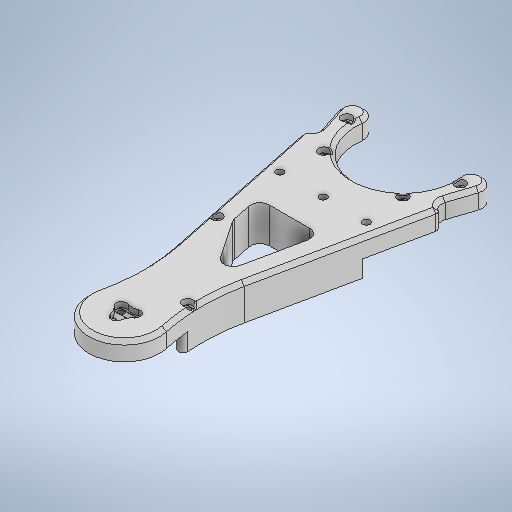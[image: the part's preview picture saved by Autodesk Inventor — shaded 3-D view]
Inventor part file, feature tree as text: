
AUTODESK INVENTOR PART (.ipt)
format: ipt  version: 2025.2 (Build 292293000, 293)  size: 1,431,040 bytes
history: native  units: mm
features: sketch x17, extrude x15, projected_geometry x11, other x8, reference x6, chamfer x2, fillet x2
ambient origin geometry x8: Origin, YZ Plane, XZ Plane, XY Plane, X Axis, Y Axis, Z Axis, Center Point
bodies: Solid1 (feature_tree)
feature tree (61):
  other  "motion_thigh_top"
  extrude  "Extrusion1"  Depth=52.1mm
  sketch  "Sketch2"  dims[d2=4.0mm d3=6.34888mm]
  extrude  "Extrusion4"  Depth=6.34888mm
  extrude  "Extrusion5"  Depth=80.799962mm
  sketch  "Sketch10"  dims[d8=5.976389mm d9=64.023611mm]
  extrude  "Extrusion8"  Depth=80.799962mm
  extrude  "Extrusion9"  Depth=64.023611mm
  extrude  "Extrusion10"  Depth=35.0mm
  chamfer  "Chamfer1"  Distance=10.137333mm
  extrude  "Extrusion20"  Depth=10.0mm
  extrude  "Extrusion21"  Depth=10.0mm
  extrude  "Extrusion22"  Depth=75.0mm
  extrude  "Extrusion23"  Depth=10.0mm TaperAngle=0.0deg
  extrude  "Extrusion24"  Depth=10.0mm
  fillet  "Fillet2"  Radius=7.05mm
  extrude  "Extrusion25"  Depth=10.0mm
  extrude  "Extrusion26"  TaperAngle=45.0deg  [1 undecoded]
  extrude  "Extrusion27"  Depth=10.0mm
  fillet  "Fillet3"  Radius=5.6mm
  extrude  "Extrusion28"  Depth=10.0mm
  chamfer  "Chamfer2"  Distance=5.6mm
  sketch  "Sketch1"  dims[d0=3.0mm d1=52.1mm]
  sketch  "Sketch4"  dims[d4=18.882403mm d5=80.799962mm]
  sketch  "Sketch5"  dims[d6=68.556751mm d7=80.799962mm]
  sketch  "Sketch11"  dims[d10=35.0mm d11=35.0mm]
  reference  "Reference11"
  sketch  "Sketch12"  dims[d12=64.023611mm]
  reference  "Reference12"
  reference  "Reference13"
  sketch  "Sketch13"  dims[d13=5.976389mm]
  sketch  "Sketch24"  dims[d14=8.056861mm]
  reference  "Reference20"
  reference  "Reference21"
  projected_geometry  "Projected Loop2"
  sketch  "Sketch25"  dims[d15=48.480908mm]
  reference  "Reference22"
  projected_geometry  "Projected Loop3"
  sketch  "Sketch26"  dims[d16=48.480908mm]
  sketch  "Sketch27"  dims[d17=8.056861mm]
  sketch  "Sketch28"  dims[d18=10.137333mm]
  projected_geometry  "Projected Loop4"
  sketch  "Sketch29"  dims[d19=32.938205mm]
  sketch  "Sketch30"  dims[d20=21.537769mm]
  projected_geometry  "Projected Loop5"
  sketch  "Sketch31"  dims[d21=21.537769mm]
  projected_geometry  "Projected Loop6"
  projected_geometry  "Projected Loop7"
  projected_geometry  "Projected Loop8"
  projected_geometry  "Projected Loop9"
  projected_geometry  "Projected Loop10"
  projected_geometry  "Projected Loop11"
  sketch  "Sketch32"  dims[d22=32.938205mm d23=10.137333mm d24=150.0mm d25=38.0mm d26=75.0mm d28=10.0mm d29=0.0mm d30=48.0mm d31=7.05mm d32=7.05mm d33=45.0deg d40=17.0mm d41=5.6mm d44=5.6mm d45=5.6mm d46=2.8mm d47=2.8mm d48=2.8mm d50=8.5mm d51=3.0mm d52=0.0mm d53=3.0mm d54=3.0mm d55=3.0mm d56=0.0mm d57=0.0mm d63=10.0mm d64=0.0mm d65=0.0mm d66=0.0mm d67=100.0mm d68=10.0mm d69=0.0mm d84=2.0mm d85=2.0mm d86=45.0deg d115=9.0mm d116=0.0mm d117=7.05mm d118=9.0mm d119=0.0mm d120=7.05mm d121=3.0mm d122=3.0mm d123=0.0mm d124=0.0mm d125=5.6mm d126=5.6mm d127=3.0mm d128=0.0mm d129=10.0mm d130=0.0mm d131=0.0mm d132=5.0mm d133=5.6mm d134=5.6mm d135=5.6mm d136=5.6mm d137=3.0mm d138=0.0mm d139=0.2mm d140=0.0mm d141=0.2mm d142=0.0mm d143=0.4mm d144=17.0mm d145=0.85mm d146=0.2mm d147=0.0mm d148=0.2mm d149=2.0mm d150=45.0deg]
  projected_geometry  "Projected Loop12"
  parser-record x2  (decoder bookkeeping rows leaked as tree rows — omitted from the tree; the rows remain in map.json)
  other  "leg_articulation_assembly.iam"
  other  "Big_drum:1"
  other  "WBR.iam"
  other  "leg_wheel:1"
  other  "leg_extend:1"
note: 1 required parameter value undecoded (feature->parameter linkage not recoverable at this tier; creation-order binding heuristic only, values carry confidence <= 0.55)
note: 2 file-system paths scrubbed to <path> (originals preserved in map.json)
